# Revit family: Domotics-DomesticRanges-GEWISS-SYSTEM_POWER-SOCKET-OUTLET_ISR_1M
name_source: partatom
category: Apparecchi elettrici
revit_build: Autodesk Revit 2016 (Build: 20161004_0715(x64)
units: mm (PartAtom-declared; Revit-internal decimal feet)

## family parameters
Condiviso = Sì
Host = Superficie
Mantenere orientamento annotazione = Sì
Numero OmniClass = 23.80.50.14
Punto di calcolo locali = No
Quota connettore circolare = Usa diametro
Taglio con vuoti quando caricato = Sì
Tipo di parte = Normale
Titolo OmniClass = Plug Connectors

## types (1)
- GW20320 - S. OUTLET 2M 2P 10A ISRAELY SY/WH
    Catalogue = DOMOTICS
    Catalogue Range = SYSTEM - DOMESTIC RANGE
    Colour = White
    Description. = Israel
    Description: = 2P - 10 A
    Descrizione = S. OUTLET 2M 2P 10A ISRAELY SY/WH
    EAN code = 8011564818019
    Electrocod = 0131
    For plug pins = Round Ã˜ 4 mm
    IDF = 91f88b9e-6881-42e4-ae49-3583b1340b71
    IDT = 0805872f-338d-4882-8bc1-e08a323adf42
    Immagine tipo = GW20320.jpg
    Larghezza presa = 23 mm  [stored 0.0754593 ft]
    Modello = GW20320
    No. SYSTEM modules = 1
    Produttore = GEWISS S.p.A.
    Prospetto di default = 1219 mm
    SEO = Socket outlet
    Simbolo = SIMBOLO PRESE : PRESA
    Technical sheet = https://www.gewiss.com
    Tipo_ = SYSTEM PRESE ISRAELE BASE : GW20320 Presa standard Israeliano 2P 10A bianco
    URL = https://www.gewiss.com
    Version file RFA = 19.4

note: [stored X ft] marks values corroborated as IEEE doubles in the binary element streams (Revit-internal decimal feet)

## geometry (parser evidence)
native form markers: Sweep x2
no freeform markers — native parametric forms only
